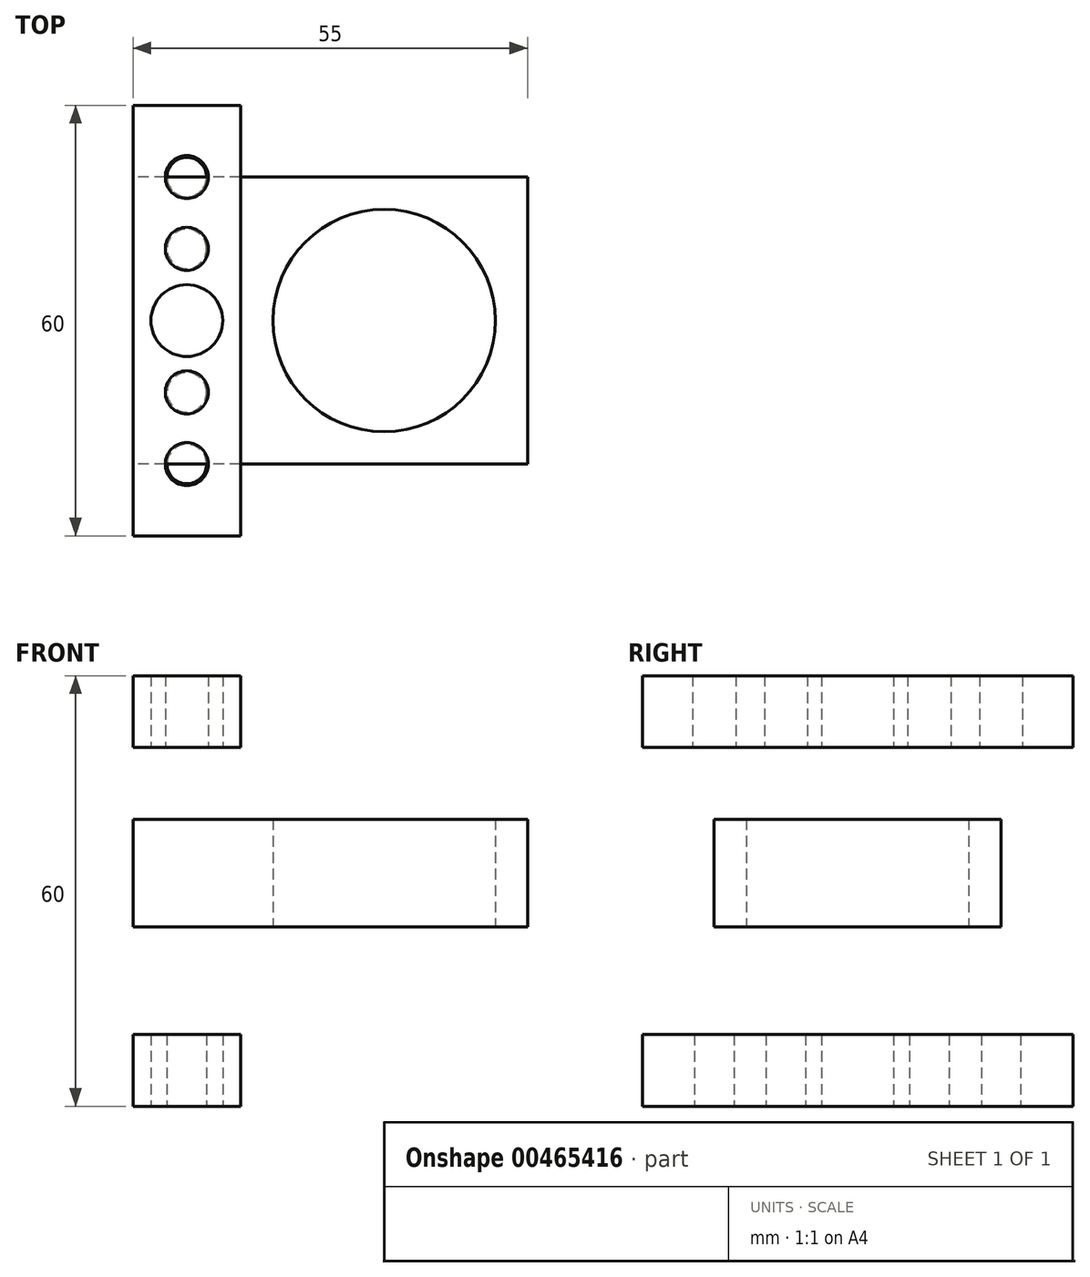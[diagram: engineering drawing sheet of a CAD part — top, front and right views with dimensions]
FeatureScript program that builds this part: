
annotation { "Feature Type Name" : "Feature", "Feature Type Description" : "" }
export const myFeature = defineFeature(function(context is Context, id is Id, definition is map)
    precondition{}
    {
        {
            var Q0;
            Q0=qCreatedBy(makeId("Top.planeOp"),FACE);
            var sketch = newSketch(context, id + "F0", { "sketchPlane" : qUnion([Q0])});
            skLineSegment(sketch, "E0.bottom", {"start": v(7.5, -30) * mm, "end": v(-7.5, -30) * mm});
            skLineSegment(sketch, "E0.top", {"start": v(7.5, 30) * mm, "end": v(-7.5, 30) * mm});
            skLineSegment(sketch, "E0.left", {"start": v(7.5, -30) * mm, "end": v(7.5, 30) * mm});
            skLineSegment(sketch, "E0.right", {"start": v(-7.5, -30) * mm, "end": v(-7.5, 30) * mm});
            skPoint(sketch, "E0.middle", {"position": v(0, 0) * mm});
            skCircle(sketch, "E1", {"center": v(0, 20) * mm, "radius": 2.75 * mm});
            skCircle(sketch, "E2", {"center": v(0, 10) * mm, "radius": 2.75 * mm});
            skCircle(sketch, "E3", {"center": v(0, 0) * mm, "radius": 5 * mm});
            skCircle(sketch, "E4", {"center": v(0, -10) * mm, "radius": 2.75 * mm});
            skCircle(sketch, "E5", {"center": v(0, -20) * mm, "radius": 2.75 * mm});
            skSolve(sketch);
        }
        {
            var Q0;
            Q0=qCreatedBy(makeId("Top.planeOp"),FACE);
            cPlane(context, id + "F1", {"entities" : qUnion([Q0]), "cplaneType" : CPlaneType.OFFSET, "offset" : 25 * mm, "width" : 150 * mm, "height" : 150 * mm});
        }
        {
            var Q0;
            Q0=qCreatedBy(makeId("Top.planeOp"),FACE);
            cPlane(context, id + "F2", {"entities" : qUnion([Q0]), "cplaneType" : CPlaneType.OFFSET, "offset" : 50 * mm, "width" : 150 * mm, "height" : 150 * mm});
        }
        {
            var Q0;
            Q0=qCreatedBy(id+"F2.planeOp",FACE);
            var sketch = newSketch(context, id + "F3", { "sketchPlane" : qUnion([Q0])});
            skLineSegment(sketch, "E6.bottom", {"start": v(7.5, -30) * mm, "end": v(-7.5, -30) * mm});
            skLineSegment(sketch, "E6.top", {"start": v(7.5, 30) * mm, "end": v(-7.5, 30) * mm});
            skLineSegment(sketch, "E6.left", {"start": v(7.5, -30) * mm, "end": v(7.5, 30) * mm});
            skLineSegment(sketch, "E6.right", {"start": v(-7.5, -30) * mm, "end": v(-7.5, 30) * mm});
            skPoint(sketch, "E6.middle", {"position": v(0, 0) * mm});
            skCircle(sketch, "E7", {"center": v(0, 20) * mm, "radius": 3 * mm});
            skCircle(sketch, "E8", {"center": v(0, 10) * mm, "radius": 3 * mm});
            skCircle(sketch, "E9", {"center": v(0, 0) * mm, "radius": 5 * mm});
            skCircle(sketch, "E10", {"center": v(0, -10) * mm, "radius": 3 * mm});
            skCircle(sketch, "E11", {"center": v(0, -20) * mm, "radius": 3 * mm});
            skSolve(sketch);
        }
        {
            var Q0;
            Q0=qCreatedBy(id+"F1.planeOp",FACE);
            var sketch = newSketch(context, id + "F4", { "sketchPlane" : qUnion([Q0])});
            skLineSegment(sketch, "E12.bottom", {"start": v(7.5, 20) * mm, "end": v(-7.5, 20) * mm});
            skLineSegment(sketch, "E12.top", {"start": v(7.5, -20) * mm, "end": v(-7.5, -20) * mm});
            skLineSegment(sketch, "E12.left", {"start": v(7.5, 20) * mm, "end": v(7.5, -20) * mm});
            skLineSegment(sketch, "E12.right", {"start": v(-7.5, 20) * mm, "end": v(-7.5, -20) * mm});
            skPoint(sketch, "E12.middle", {"position": v(0, 0) * mm});
            skLineSegment(sketch, "E13.bottom", {"start": v(7.5, -20) * mm, "end": v(47.5, -20) * mm});
            skLineSegment(sketch, "E13.top", {"start": v(7.5, 20) * mm, "end": v(47.5, 20) * mm});
            skLineSegment(sketch, "E13.left", {"start": v(7.5, -20) * mm, "end": v(7.5, 20) * mm});
            skLineSegment(sketch, "E13.right", {"start": v(47.5, -20) * mm, "end": v(47.5, 20) * mm});
            skLineSegment(sketch, "E14", {"start": v(27.5, -20) * mm, "end": v(27.5, 20) * mm, "construction": true});
            skCircle(sketch, "E15", {"center": v(27.5, 0) * mm, "radius": 15.5 * mm});
            skSolve(sketch);
        }
        {
            var Q0;
            Q0 = qSketchRegion(id + "F0", true);
            extrude(context, id + "F5", {"entities" : qUnion([Q0]), "depth" : 10 * mm});
        }
        {
            var Q0;
            Q0 = qSketchRegion(id + "F3", true);
            extrude(context, id + "F6", {"entities" : qUnion([Q0]), "depth" : 10 * mm});
        }
        {
            var Q0;
            Q0 = qSketchRegion(id + "F4", true);
            extrude(context, id + "F7", {"entities" : qUnion([Q0]), "depth" : 15 * mm});
        }
    });
